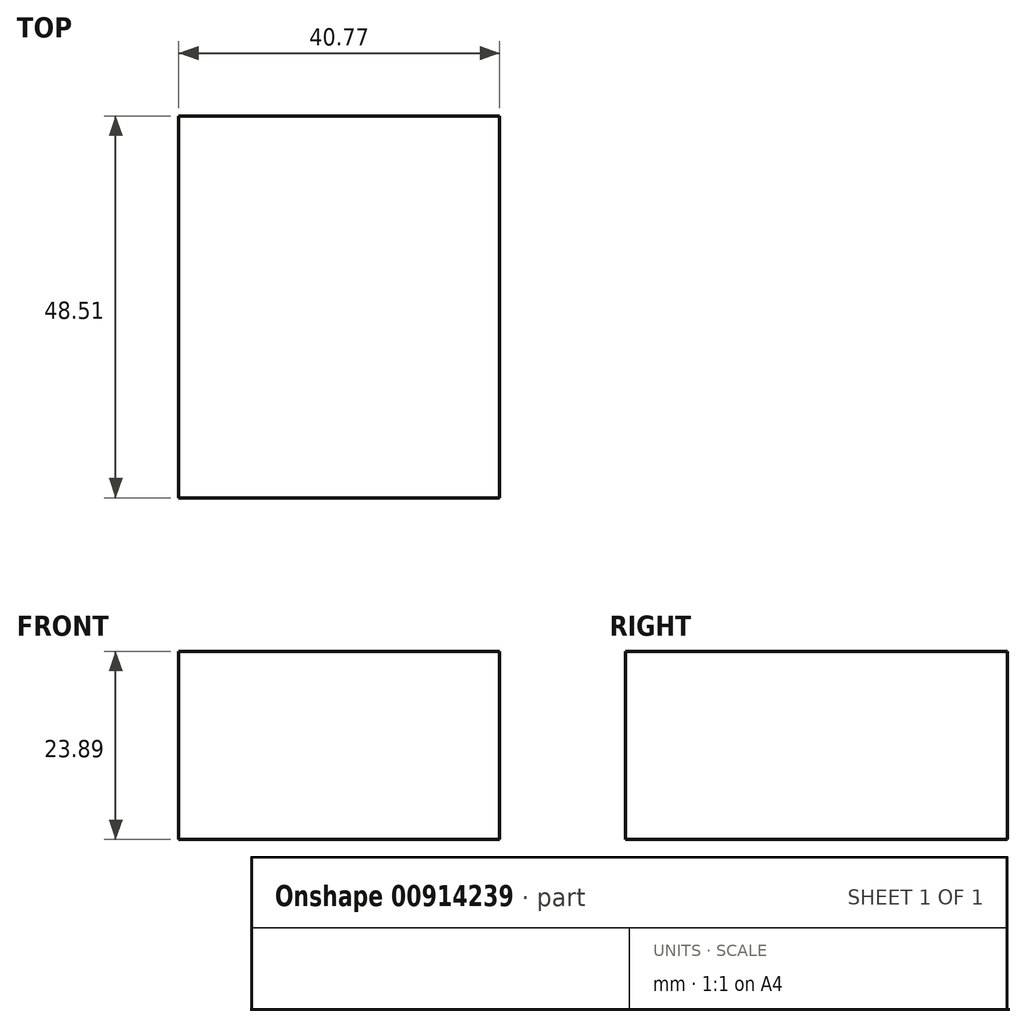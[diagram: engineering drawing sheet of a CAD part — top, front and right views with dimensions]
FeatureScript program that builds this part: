
annotation { "Feature Type Name" : "Feature", "Feature Type Description" : "" }
export const myFeature = defineFeature(function(context is Context, id is Id, definition is map)
    precondition{}
    {
        {
            var Q0;
            Q0=qCreatedBy(makeId("Front.planeOp"),FACE);
            var sketch = newSketch(context, id + "F0", { "sketchPlane" : qUnion([Q0])});
            skLineSegment(sketch, "E0.bottom", {"start": v(-60.58, 37.07) * mm, "end": v(-19.81, 37.07) * mm});
            skLineSegment(sketch, "E0.top", {"start": v(-60.58, 13.18) * mm, "end": v(-19.81, 13.18) * mm});
            skLineSegment(sketch, "E0.left", {"start": v(-60.58, 37.07) * mm, "end": v(-60.58, 13.18) * mm});
            skLineSegment(sketch, "E0.right", {"start": v(-19.81, 37.07) * mm, "end": v(-19.81, 13.18) * mm});
            skSolve(sketch);
        }
        {
            var Q0;
            Q0 = qSketchRegion(id + "F0", true);
            extrude(context, id + "F1", {"entities" : qUnion([Q0]), "oppositeDirection" : true, "depth" : 48.5 * mm, "offsetDistance" : 25.4 * mm});
        }
    });
